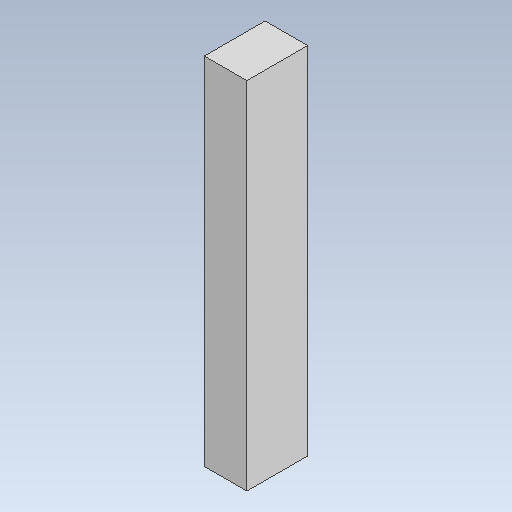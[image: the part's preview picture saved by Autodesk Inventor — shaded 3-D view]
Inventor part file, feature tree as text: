
AUTODESK INVENTOR PART (.ipt)
format: ipt  version: 2021 (Build 250183000, 183)  size: 92,160 bytes
history: native  units: mm
features: extrude x1, sketch x1
ambient origin geometry x8: Origin, YZ Plane, XZ Plane, XY Plane, X Axis, Y Axis, Z Axis, Center Point
bodies: Solid1 (feature_tree)
feature tree (2):
  extrude  "Extrusion1"  Depth=10.0mm
  sketch  "Sketch2"  dims[d2=7.0mm d3=10.0mm d4=58.493mm d5=0.0mm]
